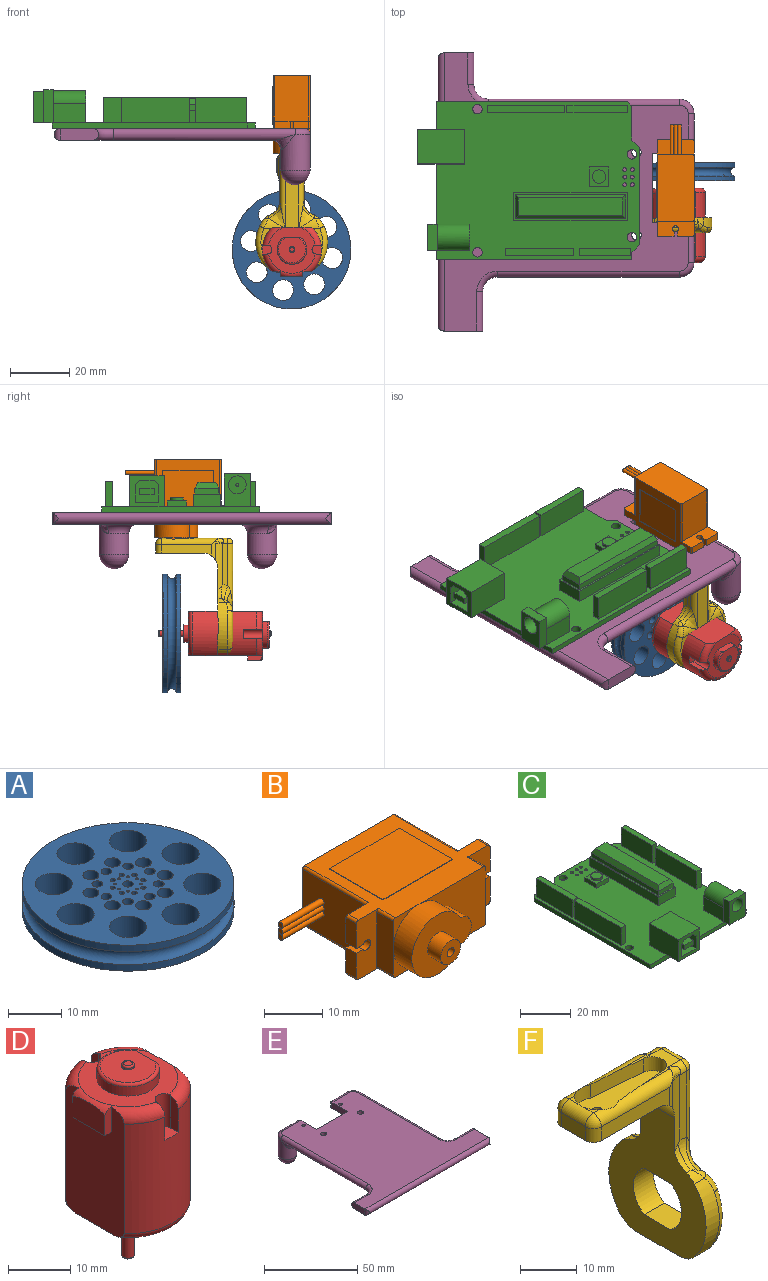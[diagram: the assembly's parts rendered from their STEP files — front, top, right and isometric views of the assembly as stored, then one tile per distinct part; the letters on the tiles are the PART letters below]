
ASSEMBLY  parts=6 mates=5
PART A: 46 faces, bbox 45.6x45.6x6 mm
  f0: cylinder r=20mm len=40mm, axis (0,0,-1), area 188.5mm2, adj f3,f45
  f1: cylinder r=20mm len=40mm, axis (0,0,-1), area 188.5mm2, adj f4,f45
  f2: cylinder r=1mm len=6mm, axis (0,0,-1), area 37.7mm2, adj f3,f4
  f3: plane 40x40mm, normal (0,0,1), area 856.1mm2, adj f0,f2,f5,f6,f7,f8,f9,f10
  f4: plane 40x40mm, normal (0,0,-1), area 856.1mm2, adj f1,f2,f5,f6,f7,f8,f9,f10
  f5: cylinder r=3.5mm len=7mm, axis (0,0,1), area 131.9mm2, adj f3,f4
  f6: cylinder r=3.5mm len=7mm, axis (0,0,1), area 131.9mm2, adj f3,f4
  f7: cylinder r=3.5mm len=7mm, axis (0,0,1), area 131.9mm2, adj f3,f4
  f8: cylinder r=3.5mm len=7mm, axis (0,0,1), area 131.9mm2, adj f3,f4
  f9: cylinder r=3.5mm len=7mm, axis (0,0,1), area 131.9mm2, adj f3,f4
  f10: cylinder r=3.5mm len=7mm, axis (0,0,1), area 131.9mm2, adj f3,f4
  f11: cylinder r=3.5mm len=7mm, axis (0,0,1), area 131.9mm2, adj f3,f4
  f12: cylinder r=3.5mm len=7mm, axis (0,0,1), area 131.9mm2, adj f3,f4
  f13: cylinder r=1.5mm len=6mm, axis (0,0,1), area 56.5mm2, adj f3,f4
  f14: cylinder r=0.5mm len=6mm, axis (0,0,1), area 18.8mm2, adj f3,f4
  f15: cylinder r=0.5mm len=6mm, axis (0,0,1), area 18.8mm2, adj f3,f4
  f16: cylinder r=0.5mm len=6mm, axis (0,0,1), area 18.8mm2, adj f3,f4
  f17: cylinder r=0.5mm len=6mm, axis (0,0,1), area 18.8mm2, adj f3,f4
  f18: cylinder r=0.5mm len=6mm, axis (0,0,1), area 18.8mm2, adj f3,f4
  f19: cylinder r=0.5mm len=6mm, axis (0,0,1), area 18.8mm2, adj f3,f4
  f20: cylinder r=0.5mm len=6mm, axis (0,0,1), area 18.8mm2, adj f3,f4
  f21: cylinder r=0.25mm len=6mm, axis (0,0,1), area 9.4mm2, adj f3,f4
  f22: cylinder r=0.25mm len=6mm, axis (0,0,1), area 9.4mm2, adj f3,f4
  f23: cylinder r=0.25mm len=6mm, axis (0,0,1), area 9.4mm2, adj f3,f4
  f24: cylinder r=0.25mm len=6mm, axis (0,0,1), area 9.4mm2, adj f3,f4
  f25: cylinder r=0.25mm len=6mm, axis (0,0,1), area 9.4mm2, adj f3,f4
  f26: cylinder r=0.25mm len=6mm, axis (0,0,1), area 9.4mm2, adj f3,f4
  f27: cylinder r=0.25mm len=6mm, axis (0,0,1), area 9.4mm2, adj f3,f4
  f28: cylinder r=0.25mm len=6mm, axis (0,0,1), area 9.4mm2, adj f3,f4
  f29: cylinder r=1.5mm len=6mm, axis (0,0,1), area 56.5mm2, adj f3,f4
  f30: cylinder r=1.5mm len=6mm, axis (0,0,1), area 56.5mm2, adj f3,f4
  f31: cylinder r=1.5mm len=6mm, axis (0,0,1), area 56.5mm2, adj f3,f4
  f32: cylinder r=1.5mm len=6mm, axis (0,0,1), area 56.5mm2, adj f3,f4
  f33: cylinder r=1.5mm len=6mm, axis (0,0,1), area 56.5mm2, adj f3,f4
  f34: cylinder r=1.5mm len=6mm, axis (0,0,1), area 56.5mm2, adj f3,f4
  f35: cylinder r=1.5mm len=6mm, axis (0,0,1), area 56.5mm2, adj f3,f4
  f36: cylinder r=1mm len=6mm, axis (0,0,1), area 37.7mm2, adj f3,f4
  f37: cylinder r=0.5mm len=6mm, axis (0,0,1), area 18.8mm2, adj f3,f4
  f38: cylinder r=1mm len=6mm, axis (0,0,1), area 37.7mm2, adj f3,f4
  f39: cylinder r=1mm len=6mm, axis (0,0,1), area 37.7mm2, adj f3,f4
  f40: cylinder r=1mm len=6mm, axis (0,0,1), area 37.7mm2, adj f3,f4
  f41: cylinder r=1mm len=6mm, axis (0,0,1), area 37.7mm2, adj f3,f4
  f42: cylinder r=1mm len=6mm, axis (0,0,1), area 37.7mm2, adj f3,f4
  f43: cylinder r=1mm len=6mm, axis (0,0,1), area 37.7mm2, adj f3,f4
  f44: cylinder r=1mm len=6mm, axis (0,0,1), area 37.7mm2, adj f3,f4
  f45: torus R=20mm, axis (0,0,1), area 563.9mm2, adj f0,f1
PART B: 59 faces, bbox 37.5x29.7x12.7 mm
  f0: plane 31.5x22mm, normal (0,0,-1), area 277mm2, adj f1,f3,f4,f15,f16,f17,f23,f25
  f1: cylinder r=0.5mm len=4mm, axis (0,-1,0), area 3.1mm2, adj f0,f3,f20,f23
  f2: plane 6.25x6.25mm, normal (0,-1,0), area 8.3mm2, adj f5,f7,f18,f47
  f3: plane 16.25x12.5mm, normal (0,-1,0), area 132.6mm2, adj f0,f1,f18,f20,f22,f47,f48
  f4: plane 6.25x6.25mm, normal (0,-1,0), area 8.3mm2, adj f0,f7,f34,f47
  f5: cylinder r=0.5mm len=4mm, axis (0,-1,0), area 3.1mm2, adj f2,f7,f18,f33
  f6: plane 15.5x11.5mm, normal (-1,0,0), area 174.9mm2, adj f8,f12,f13,f14,f15,f16,f17
  f7: plane 11.5x4mm, normal (-1,0,0), area 46mm2, adj f2,f4,f5,f33,f34
  f8: cylinder r=0.6mm len=10mm, axis (-1,0,0), area 37.7mm2, adj f6,f9
  f9: plane 1.2x1.2mm, normal (-1,0,0), area 1.1mm2, adj f8
  f10: plane 1.2x1.2mm, normal (-1,0,0), area 1.1mm2, adj f12
  f11: plane 1.2x1.2mm, normal (-1,0,0), area 1.1mm2, adj f13
  f12: cylinder r=0.6mm len=10mm, axis (-1,0,0), area 37.7mm2, adj f6,f10
  f13: cylinder r=0.6mm len=10mm, axis (-1,0,0), area 37.7mm2, adj f6,f11
  f14: cylinder r=0.5mm len=15.5mm, axis (0,-1,0), area 12.2mm2, adj f6,f15,f17,f18
  f15: plane 22.5x12.5mm, normal (0,1,0), area 281mm2, adj f0,f6,f14,f16,f18,f19,f21,f26
  f16: cylinder r=0.5mm len=15.5mm, axis (0,1,0), area 12.2mm2, adj f0,f6,f15,f17
  f17: plane 12.5x5.5mm, normal (0,1,0), area 57.8mm2, adj f0,f6,f14,f16,f18,f35,f36,f37
  f18: plane 31.5x22mm, normal (0,0,1), area 277mm2, adj f2,f3,f5,f14,f15,f17,f19,f22
  f19: cylinder r=0.5mm len=15.5mm, axis (0,1,0), area 12.2mm2, adj f15,f18,f21,f25
  f20: plane 11.5x4mm, normal (1,0,0), area 46mm2, adj f1,f3,f22,f23
  f21: plane 15.5x11.5mm, normal (1,0,0), area 178.2mm2, adj f15,f19,f25,f26
  f22: cylinder r=0.5mm len=4mm, axis (0,1,0), area 3.1mm2, adj f3,f18,f20,f23
  f23: plane 12.5x5.5mm, normal (0,-1,0), area 57.8mm2, adj f0,f1,f18,f20,f22,f24,f27,f28
  f24: cylinder r=0.5mm len=2.5mm, axis (0,1,0), area 2mm2, adj f18,f23,f25,f28
  f25: plane 12.5x5.5mm, normal (0,1,0), area 57.8mm2, adj f0,f18,f19,f21,f24,f26,f27,f28
  f26: cylinder r=0.5mm len=15.5mm, axis (0,-1,0), area 12.2mm2, adj f0,f15,f21,f25
  f27: cylinder r=0.5mm len=2.5mm, axis (0,-1,0), area 2mm2, adj f0,f23,f25,f29
  f28: plane 5.25x2.5mm, normal (1,0,0), area 13.1mm2, adj f23,f24,f25,f30
  f29: plane 5.25x2.5mm, normal (1,0,0), area 13.1mm2, adj f23,f25,f27,f32
  f30: plane 2.5x1.63mm, normal (0,0,-1), area 4.1mm2, adj f23,f25,f28,f31
  f31: cylinder r=1mm len=2.5mm, axis (0,-1,0), area 13.1mm2, adj f23,f25,f30,f32
  f32: plane 2.5x1.63mm, normal (0,0,1), area 4.1mm2, adj f23,f25,f29,f31
  f33: plane 12.5x5.5mm, normal (0,-1,0), area 57.8mm2, adj f0,f5,f7,f18,f34,f35,f36,f37
  f34: cylinder r=0.5mm len=4mm, axis (0,1,0), area 3.1mm2, adj f0,f4,f7,f33
  f35: cylinder r=0.5mm len=2.5mm, axis (0,1,0), area 2mm2, adj f0,f17,f33,f37
  f36: plane 5.25x2.5mm, normal (-1,0,0), area 13.1mm2, adj f17,f33,f38,f39
  f37: plane 5.25x2.5mm, normal (-1,0,0), area 13.1mm2, adj f17,f33,f35,f41
  f38: cylinder r=0.5mm len=2.5mm, axis (0,-1,0), area 2mm2, adj f17,f18,f33,f36
  f39: plane 2.5x1.63mm, normal (0,0,-1), area 4.1mm2, adj f17,f33,f36,f40
  f40: cylinder r=1mm len=2.5mm, axis (0,-1,0), area 13.1mm2, adj f17,f33,f39,f41
  f41: plane 2.5x1.63mm, normal (0,0,1), area 4.1mm2, adj f17,f33,f37,f40
  f42: plane 13x0.1mm, normal (-1,0,0), area 1.3mm2, adj f18,f43,f45,f46
  f43: plane 17x0.1mm, normal (0,1,0), area 1.7mm2, adj f18,f42,f44,f46
  f44: plane 13x0.1mm, normal (1,0,0), area 1.3mm2, adj f18,f43,f45,f46
  f45: plane 17x0.1mm, normal (0,-1,0), area 1.7mm2, adj f18,f42,f44,f46
  f46: plane 17x13mm, normal (0,0,1), area 221mm2, adj f42,f43,f44,f45
  f47: cylinder r=6.25mm len=12.5mm, axis (0,-1,0), area 150.6mm2, adj f2,f3,f4,f48,f49
  f48: cylinder r=2.8mm len=5.59mm, axis (0,-1,0), area 38.3mm2, adj f3,f47,f49
  f49: plane 14.5x12.5mm, normal (0,-1,0), area 113.7mm2, adj f47,f48,f51
  f50: plane 1.7x1.7mm, normal (0,-1,0), area 2.3mm2, adj f53
  f51: cylinder r=2.4mm len=4.8mm, axis (0,-1,0), area 48.3mm2, adj f49,f52
  f52: plane 4.8x4.8mm, normal (0,-1,0), area 15.8mm2, adj f51,f53
  f53: cylinder r=0.85mm len=3.2mm, axis (0,-1,0), area 17.1mm2, adj f50,f52
  f54: plane 13x0.1mm, normal (-1,0,0), area 1.3mm2, adj f0,f55,f56,f57
  f55: plane 17x0.1mm, normal (0,1,0), area 1.7mm2, adj f0,f54,f56,f58
  f56: plane 17x13mm, normal (0,0,-1), area 221mm2, adj f54,f55,f57,f58
  f57: plane 17x0.1mm, normal (0,-1,0), area 1.7mm2, adj f0,f54,f56,f58
  f58: plane 13x0.1mm, normal (1,0,0), area 1.3mm2, adj f0,f55,f56,f57
PART C: 159 faces, bbox 53.3x75x13 mm
  f0: plane 68.58x53.34mm, normal (0,0,1), area 2744.3mm2, adj f1,f2,f3,f4,f5,f6,f7,f8
  f1: plane 2.54x2.54mm, normal (0.71,0.71,0), area 6.8mm2, adj f0,f2,f51,f52
  f2: plane 32.77x1.9mm, normal (0,1,0), area 62.3mm2, adj f0,f1,f3,f52
  f3: plane 2.54x2.54mm, normal (-0.71,0.71,0), area 6.8mm2, adj f0,f2,f4,f52
  f4: plane 11.43x1.9mm, normal (0,1,0), area 21.7mm2, adj f0,f3,f5,f52
  f5: plane 1.9x1.52mm, normal (-0.71,0.71,0), area 4.1mm2, adj f0,f4,f6,f52
  f6: plane 64.52x1.9mm, normal (-1,0,0), area 122.6mm2, adj f0,f5,f7,f52
  f7: plane 53.34x1.9mm, normal (0,-1,0), area 101.3mm2, adj f0,f6,f8,f52,f81,f99,f107,f108
  f8: plane 66.04x1.9mm, normal (1,0,0), area 125.5mm2, adj f0,f7,f51,f52
  f9: cylinder r=1.59mm len=3.18mm, axis (0,0,-1), area 19mm2, adj f0,f52
  f10: cylinder r=1.59mm len=3.18mm, axis (0,0,-1), area 19mm2, adj f0,f52
  f11: cylinder r=1.59mm len=3.18mm, axis (0,0,-1), area 19mm2, adj f0,f52
  f12: cylinder r=1.59mm len=3.18mm, axis (0,0,-1), area 19mm2, adj f0,f52
  f13: cylinder r=0.64mm len=1.9mm, axis (0,0,-1), area 7.6mm2, adj f52,f80
  f14: cylinder r=0.64mm len=1.9mm, axis (0,0,-1), area 7.6mm2, adj f52,f79
  f15: cylinder r=0.64mm len=1.9mm, axis (0,0,-1), area 7.6mm2, adj f52,f78
  f16: cylinder r=0.64mm len=1.9mm, axis (0,0,-1), area 7.6mm2, adj f52,f77
  f17: cylinder r=0.64mm len=1.9mm, axis (0,0,-1), area 7.6mm2, adj f52,f76
  f18: cylinder r=0.64mm len=1.9mm, axis (0,0,-1), area 7.6mm2, adj f52,f75
  f19: cylinder r=0.64mm len=1.9mm, axis (0,0,-1), area 7.6mm2, adj f52,f74
  f20: cylinder r=0.64mm len=1.9mm, axis (0,0,-1), area 7.6mm2, adj f52,f73
  f21: cylinder r=0.64mm len=1.9mm, axis (0,0,-1), area 7.6mm2, adj f52,f72
  f22: cylinder r=0.64mm len=1.9mm, axis (0,0,-1), area 7.6mm2, adj f52,f71
  f23: cylinder r=0.64mm len=1.9mm, axis (0,0,-1), area 7.6mm2, adj f52,f58
  f24: cylinder r=0.64mm len=1.9mm, axis (0,0,-1), area 7.6mm2, adj f52,f140
  f25: cylinder r=0.64mm len=1.9mm, axis (0,0,-1), area 7.6mm2, adj f52,f151
  f26: cylinder r=0.64mm len=1.9mm, axis (0,0,-1), area 7.6mm2, adj f52,f59
  f27: cylinder r=0.64mm len=1.9mm, axis (0,0,-1), area 7.6mm2, adj f52,f60
  f28: cylinder r=0.64mm len=1.9mm, axis (0,0,-1), area 7.6mm2, adj f52,f61
  f29: cylinder r=0.64mm len=1.9mm, axis (0,0,-1), area 7.6mm2, adj f52,f62
  f30: cylinder r=0.64mm len=1.9mm, axis (0,0,-1), area 7.6mm2, adj f52,f63
  f31: cylinder r=0.64mm len=1.9mm, axis (0,0,-1), area 7.6mm2, adj f52,f64
  f32: cylinder r=0.64mm len=1.9mm, axis (0,0,-1), area 7.6mm2, adj f52,f65
  f33: cylinder r=0.64mm len=1.9mm, axis (0,0,-1), area 7.6mm2, adj f52,f139
  f34: cylinder r=0.64mm len=1.9mm, axis (0,0,-1), area 7.6mm2, adj f52,f138
  f35: cylinder r=0.64mm len=1.9mm, axis (0,0,-1), area 7.6mm2, adj f52,f137
  f36: cylinder r=0.64mm len=1.9mm, axis (0,0,-1), area 7.6mm2, adj f52,f136
  f37: cylinder r=0.64mm len=1.9mm, axis (0,0,-1), area 7.6mm2, adj f52,f135
  f38: cylinder r=0.64mm len=1.9mm, axis (0,0,-1), area 7.6mm2, adj f52,f134
  f39: cylinder r=0.64mm len=1.9mm, axis (0,0,-1), area 7.6mm2, adj f52,f133
  f40: cylinder r=0.64mm len=1.9mm, axis (0,0,-1), area 7.6mm2, adj f52,f150
  f41: cylinder r=0.64mm len=1.9mm, axis (0,0,-1), area 7.6mm2, adj f52,f149
  f42: cylinder r=0.64mm len=1.9mm, axis (0,0,-1), area 7.6mm2, adj f52,f148
  f43: cylinder r=0.64mm len=1.9mm, axis (0,0,-1), area 7.6mm2, adj f52,f147
  f44: cylinder r=0.64mm len=1.9mm, axis (0,0,-1), area 7.6mm2, adj f52,f146
  f45: cylinder r=0.64mm len=1.9mm, axis (0,0,-1), area 7.6mm2, adj f0,f52
  f46: cylinder r=0.64mm len=1.9mm, axis (0,0,-1), area 7.6mm2, adj f0,f52
  f47: cylinder r=0.64mm len=1.9mm, axis (0,0,-1), area 7.6mm2, adj f0,f52
  f48: cylinder r=0.64mm len=1.9mm, axis (0,0,-1), area 7.6mm2, adj f0,f52
  f49: cylinder r=0.64mm len=1.9mm, axis (0,0,-1), area 7.6mm2, adj f0,f52
  f50: cylinder r=0.64mm len=1.9mm, axis (0,0,-1), area 7.6mm2, adj f0,f52
  f51: plane 2.54x1.9mm, normal (0,1,0), area 4.8mm2, adj f0,f1,f8,f52
  f52: plane 68.58x53.34mm, normal (0,0,-1), area 3531.3mm2, adj f1,f2,f3,f4,f5,f6,f7,f8
  f53: plane 20.48x2.5mm, normal (0,0,1), area 51.2mm2, adj f54,f55,f56,f57
  f54: plane 8.6x2.5mm, normal (0,1,0), area 21.5mm2, adj f0,f53,f55,f57
  f55: plane 20.48x8.6mm, normal (1,0,0), area 176.1mm2, adj f0,f53,f54,f56
  f56: plane 8.6x2.5mm, normal (0,-1,0), area 21.5mm2, adj f0,f53,f55,f57
  f57: plane 20.48x8.6mm, normal (-1,0,0), area 176.1mm2, adj f0,f53,f54,f56
  f58: plane 1.27x1.27mm, normal (0,0,-1), area 1.3mm2, adj f23
  f59: plane 1.27x1.27mm, normal (0,0,-1), area 1.3mm2, adj f26
  f60: plane 1.27x1.27mm, normal (0,0,-1), area 1.3mm2, adj f27
  f61: plane 1.27x1.27mm, normal (0,0,-1), area 1.3mm2, adj f28
  f62: plane 1.27x1.27mm, normal (0,0,-1), area 1.3mm2, adj f29
  f63: plane 1.27x1.27mm, normal (0,0,-1), area 1.3mm2, adj f30
  f64: plane 1.27x1.27mm, normal (0,0,-1), area 1.3mm2, adj f31
  f65: plane 1.27x1.27mm, normal (0,0,-1), area 1.3mm2, adj f32
  f66: plane 26x2.5mm, normal (0,0,1), area 65mm2, adj f67,f68,f69,f70
  f67: plane 26x8.6mm, normal (1,0,0), area 223.6mm2, adj f0,f66,f68,f70
  f68: plane 8.6x2.5mm, normal (0,-1,0), area 21.5mm2, adj f0,f66,f67,f69
  f69: plane 26x8.6mm, normal (-1,0,0), area 223.6mm2, adj f0,f66,f68,f70
  f70: plane 8.6x2.5mm, normal (0,1,0), area 21.5mm2, adj f0,f66,f67,f69
  f71: plane 1.27x1.27mm, normal (0,0,-1), area 1.3mm2, adj f22
  f72: plane 1.27x1.27mm, normal (0,0,-1), area 1.3mm2, adj f21
  f73: plane 1.27x1.27mm, normal (0,0,-1), area 1.3mm2, adj f20
  f74: plane 1.27x1.27mm, normal (0,0,-1), area 1.3mm2, adj f19
  f75: plane 1.27x1.27mm, normal (0,0,-1), area 1.3mm2, adj f18
  f76: plane 1.27x1.27mm, normal (0,0,-1), area 1.3mm2, adj f17
  f77: plane 1.27x1.27mm, normal (0,0,-1), area 1.3mm2, adj f16
  f78: plane 1.27x1.27mm, normal (0,0,-1), area 1.3mm2, adj f15
  f79: plane 1.27x1.27mm, normal (0,0,-1), area 1.3mm2, adj f14
  f80: plane 1.27x1.27mm, normal (0,0,-1), area 1.3mm2, adj f13
  f81: plane 11.6x6.38mm, normal (0,0,-1), area 73.9mm2, adj f7,f82,f83,f85
  f82: plane 11.6x10.5mm, normal (0,-1,0), area 64.6mm2, adj f81,f83,f85,f86,f87,f88,f89,f90
  f83: plane 16x10.5mm, normal (1,0,0), area 168mm2, adj f0,f81,f82,f84,f86
  f84: plane 11.6x10.5mm, normal (0,1,0), area 121.8mm2, adj f0,f83,f85,f86
  f85: plane 16x10.5mm, normal (-1,0,0), area 168mm2, adj f0,f81,f82,f84,f86
  f86: plane 16x11.6mm, normal (0,0,1), area 185.6mm2, adj f82,f83,f84,f85
  f87: plane 14.14x5.02mm, normal (0,0,-1), area 71mm2, adj f82,f88,f92,f93
  f88: plane 14.14x1.44mm, normal (0.71,0,-0.71), area 28.8mm2, adj f82,f87,f89,f93
  f89: plane 14.14x6.06mm, normal (1,0,0), area 85.7mm2, adj f82,f88,f90,f93
  f90: plane 14.14x7.9mm, normal (0,0,1), area 111.7mm2, adj f82,f89,f91,f93
  f91: plane 14.14x6.06mm, normal (-1,0,0), area 85.7mm2, adj f82,f90,f92,f93
  f92: plane 14.14x1.44mm, normal (-0.71,0,-0.71), area 28.8mm2, adj f82,f87,f91,f93
  f93: plane 7.9x7.5mm, normal (0,-1,0), area 47mm2, adj f87,f88,f89,f90,f91,f92,f95,f96
  f94: plane 4.88x2.08mm, normal (0,-1,0), area 10.2mm2, adj f95,f96,f97,f98
  f95: plane 14.14x4.88mm, normal (0,0,1), area 69mm2, adj f93,f94,f96,f98
  f96: plane 14.14x2.08mm, normal (-1,0,0), area 29.4mm2, adj f93,f94,f95,f97
  f97: plane 14.14x4.88mm, normal (0,0,-1), area 69mm2, adj f93,f94,f96,f98
  f98: plane 14.14x2.08mm, normal (1,0,0), area 29.4mm2, adj f93,f94,f95,f97
  f99: plane 8.88x2.88mm, normal (0,0,-1), area 25.5mm2, adj f7,f107,f108,f109
  f100: plane 11x6.49mm, normal (1,0,0), area 71.4mm2, adj f0,f101,f103,f104
  f101: cylinder r=4.44mm len=11mm, axis (0,-1,0), area 153.4mm2, adj f100,f102,f103,f104,f105
  f102: plane 11x6.49mm, normal (-1,0,0), area 71.4mm2, adj f0,f101,f103,f105
  f103: plane 10.93x8.88mm, normal (0,1,0), area 88.6mm2, adj f0,f100,f101,f102
  f104: plane 6.63x0mm, normal (0,-1,0), area 0mm2, adj f0,f100,f101,f108
  f105: plane 11.12x8.88mm, normal (0,1,0), area 10.1mm2, adj f0,f101,f102,f106,f107,f108
  f106: plane 8.88x3.3mm, normal (0,0,1), area 29.3mm2, adj f105,f107,f108,f109
  f107: plane 11.13x3.3mm, normal (-1,0,0), area 36.7mm2, adj f0,f7,f99,f105,f106,f109
  f108: plane 11.13x3.3mm, normal (1,0,0), area 36.7mm2, adj f0,f7,f99,f104,f105,f106,f109
  f109: plane 11.13x8.88mm, normal (0,-1,0), area 70.5mm2, adj f99,f106,f107,f108,f110
  f110: cylinder r=3mm len=12.8mm, axis (0,-1,0), area 241.3mm2, adj f109,f111
  f111: plane 6x6mm, normal (0,-1,0), area 27.5mm2, adj f110,f112
  f112: cylinder r=0.5mm len=10mm, axis (0,1,0), area 31.4mm2, adj f111,f113
  f113: sphere r=0.5mm, area 1.6mm2, adj f112
  f114: plane 9.33x4.3mm, normal (0,-1,0), area 40.1mm2, adj f0,f115,f117,f118
  f115: plane 38.37x4.3mm, normal (1,0,0), area 164.8mm2, adj f0,f114,f116,f118
  f116: plane 9.33x4.3mm, normal (0,1,0), area 40.1mm2, adj f0,f115,f117,f118
  f117: plane 38.37x4.3mm, normal (-1,0,0), area 164.8mm2, adj f0,f114,f116,f118
  f118: plane 38.37x9.33mm, normal (0,0,1), area 57.4mm2, adj f114,f115,f116,f117,f119,f120,f121,f122
  f119: plane 37.19x2mm, normal (-1,0,0), area 74.4mm2, adj f118,f120,f122,f127
  f120: plane 8.08x2mm, normal (0,-1,0), area 16.2mm2, adj f118,f119,f121,f126
  f121: plane 37.19x2mm, normal (1,0,0), area 74.4mm2, adj f118,f120,f122,f125
  f122: plane 8.08x2mm, normal (0,1,0), area 16.2mm2, adj f118,f119,f121,f124
  f123: plane 35.16x6.05mm, normal (0,0,1), area 212.7mm2, adj f124,f125,f126,f127
  f124: plane 8.08x2mm, normal (0,0.9,0.44), area 15.7mm2, adj f122,f123,f125,f127
  f125: plane 37.19x2mm, normal (0.89,0,0.45), area 81.1mm2, adj f121,f123,f124,f126
  f126: plane 8.08x2mm, normal (0,-0.88,0.47), area 16mm2, adj f120,f123,f125,f127
  f127: plane 37.19x2mm, normal (-0.89,0,0.45), area 81.2mm2, adj f119,f123,f124,f126
  f128: plane 23x2.44mm, normal (0,0,1), area 56mm2, adj f129,f130,f131,f132
  f129: plane 23x8.6mm, normal (1,0,0), area 197.8mm2, adj f0,f128,f130,f132
  f130: plane 8.6x2.44mm, normal (0,-1,0), area 20.9mm2, adj f0,f128,f129,f131
  f131: plane 23x8.6mm, normal (-1,0,0), area 197.8mm2, adj f0,f128,f130,f132
  f132: plane 8.6x2.44mm, normal (0,1,0), area 20.9mm2, adj f0,f128,f129,f131
  f133: plane 1.27x1.27mm, normal (0,0,-1), area 1.3mm2, adj f39
  f134: plane 1.27x1.27mm, normal (0,0,-1), area 1.3mm2, adj f38
  f135: plane 1.27x1.27mm, normal (0,0,-1), area 1.3mm2, adj f37
  f136: plane 1.27x1.27mm, normal (0,0,-1), area 1.3mm2, adj f36
  f137: plane 1.27x1.27mm, normal (0,0,-1), area 1.3mm2, adj f35
  f138: plane 1.27x1.27mm, normal (0,0,-1), area 1.3mm2, adj f34
  f139: plane 1.27x1.27mm, normal (0,0,-1), area 1.3mm2, adj f33
  f140: plane 1.27x1.27mm, normal (0,0,-1), area 1.3mm2, adj f24
  f141: plane 17.27x2.44mm, normal (0,0,1), area 42.1mm2, adj f142,f143,f144,f145
  f142: plane 8.6x2.44mm, normal (0,-1,0), area 20.9mm2, adj f0,f141,f143,f145
  f143: plane 17.27x8.6mm, normal (-1,0,0), area 148.6mm2, adj f0,f141,f142,f144
  f144: plane 8.6x2.44mm, normal (0,1,0), area 20.9mm2, adj f0,f141,f143,f145
  f145: plane 17.27x8.6mm, normal (1,0,0), area 148.6mm2, adj f0,f141,f142,f144
  f146: plane 1.27x1.27mm, normal (0,0,-1), area 1.3mm2, adj f44
  f147: plane 1.27x1.27mm, normal (0,0,-1), area 1.3mm2, adj f43
  f148: plane 1.27x1.27mm, normal (0,0,-1), area 1.3mm2, adj f42
  f149: plane 1.27x1.27mm, normal (0,0,-1), area 1.3mm2, adj f41
  f150: plane 1.27x1.27mm, normal (0,0,-1), area 1.3mm2, adj f40
  f151: plane 1.27x1.27mm, normal (0,0,-1), area 1.3mm2, adj f25
  f152: plane 6.5x2mm, normal (-1,0,0), area 13mm2, adj f0,f153,f155,f156
  f153: plane 6.5x2mm, normal (0,-1,0), area 13mm2, adj f0,f152,f154,f156
  f154: plane 6.5x2mm, normal (1,0,0), area 13mm2, adj f0,f153,f155,f156
  f155: plane 6.5x2mm, normal (0,1,0), area 13mm2, adj f0,f152,f154,f156
  f156: plane 6.5x6.5mm, normal (0,0,1), area 26.4mm2, adj f152,f153,f154,f155,f157
  f157: cylinder r=2.24mm len=4.49mm, axis (0,0,-1), area 14.1mm2, adj f156,f158
  f158: plane 4.49x4.49mm, normal (0,0,1), area 15.8mm2, adj f157
PART D: 35 faces, bbox 21.1x21.8x38 mm
  f0: plane 15.74x15.5mm, normal (0,0,1), area 119.4mm2, adj f4,f10,f11,f22,f26,f29,f30,f31
  f1: cylinder r=10mm len=21.5mm, axis (0,0,-1), area 351.1mm2, adj f4,f5,f23,f24,f25,f27,f29,f30
  f2: plane 17x15mm, normal (0,0,-1), area 187.9mm2, adj f4,f5,f6,f27,f28
  f3: cylinder r=10mm len=21.5mm, axis (0,0,-1), area 351.1mm2, adj f4,f5,f19,f20,f21,f28,f30,f31
  f4: plane 25x13.23mm, normal (1,0,0), area 326.4mm2, adj f0,f1,f2,f3,f27,f28,f29,f31
  f5: plane 24.97x13.23mm, normal (-1,0,0), area 289.4mm2, adj f1,f2,f3,f15,f17,f18,f27,f28
  f6: cylinder r=3mm len=6mm, axis (0,0,1), area 28.3mm2, adj f2,f7
  f7: plane 6x6mm, normal (0,0,-1), area 25.1mm2, adj f6,f8
  f8: cylinder r=1mm len=8.2mm, axis (0,0,1), area 51.5mm2, adj f7,f33
  f9: plane 1.4x1.4mm, normal (0,0,-1), area 1.5mm2, adj f33
  f10: plane 6x2.3mm, normal (1,0,0), area 13.6mm2, adj f0,f11,f12,f34
  f11: cylinder r=5mm len=10mm, axis (0,0,-1), area 45mm2, adj f0,f10,f34
  f12: plane 9x8.5mm, normal (0,0,1), area 59.1mm2, adj f10,f13,f34
  f13: cylinder r=1mm len=2mm, axis (0,0,-1), area 1.9mm2, adj f12,f32
  f14: plane 1.4x1.4mm, normal (0,0,1), area 1.5mm2, adj f32
  f15: plane 5.11x1.64mm, normal (0,1,0), area 7mm2, adj f5,f16,f18,f30
  f16: plane 7.4x4.73mm, normal (-1,0,0), area 33.6mm2, adj f15,f17,f18,f30
  f17: plane 5.11x1.64mm, normal (0,-1,0), area 7mm2, adj f5,f16,f18,f30
  f18: plane 7.4x1.5mm, normal (0,0,-1), area 11.1mm2, adj f5,f15,f16,f17
  f19: plane 6.6x1.78mm, normal (-1,0,0), area 9.8mm2, adj f3,f21,f22,f31
  f20: plane 6.6x1.78mm, normal (1,0,0), area 9.8mm2, adj f3,f21,f22,f30
  f21: plane 3.25x3mm, normal (0,0,1), area 8.7mm2, adj f3,f19,f20,f22
  f22: cylinder r=1.5mm len=6.5mm, axis (0,0,1), area 30.6mm2, adj f0,f19,f20,f21,f30,f31
  f23: plane 6.6x1.78mm, normal (1,0,0), area 9.8mm2, adj f1,f25,f26,f30
  f24: plane 6.6x1.78mm, normal (-1,0,0), area 9.8mm2, adj f1,f25,f26,f29
  f25: plane 3.25x3mm, normal (0,0,1), area 8.7mm2, adj f1,f23,f24,f26
  f26: cylinder r=1.5mm len=6.5mm, axis (0,0,1), area 30.6mm2, adj f0,f23,f24,f25,f29,f30
  f27: torus R=8.5mm, axis (0,0,1), area 41mm2, adj f1,f2,f4,f5
  f28: torus R=8.5mm, axis (0,0,1), area 41mm2, adj f2,f3,f4,f5
  f29: torus R=8mm, axis (0,0,1), area 22.8mm2, adj f0,f1,f4,f24,f26
  f30: torus R=8mm, axis (0,0,1), area 55.9mm2, adj f0,f1,f3,f5,f15,f16,f17,f20
  f31: torus R=8mm, axis (0,0,1), area 22.8mm2, adj f0,f3,f4,f19,f22
  f32: torus R=0.7mm, axis (0,0,1), area 2.6mm2, adj f13,f14
  f33: torus R=0.7mm, axis (0,0,-1), area 2.6mm2, adj f8,f9
  f34: torus R=4.5mm, axis (0,0,1), area 19.3mm2, adj f10,f11,f12
PART E: 36 faces, bbox 93.8x86.7x19 mm
  f0: plane 93.76x82.29mm, normal (0,0,-1), area 4476.7mm2, adj f1,f2,f3,f4,f5,f6,f7,f11
  f1: plane 13x4mm, normal (1,0,0), area 50.3mm2, adj f0,f8,f20,f27
  f2: plane 12x4mm, normal (-1,0,0), area 48mm2, adj f0,f3,f8,f15
  f3: plane 23.5x4mm, normal (0,1,0), area 94mm2, adj f0,f2,f4,f8
  f4: plane 12x4mm, normal (1,0,0), area 48mm2, adj f0,f3,f8,f22
  f5: cylinder r=1mm len=4mm, axis (0,0,-1), area 25.1mm2, adj f0,f8
  f6: plane 10.06x4mm, normal (-1,0,0), area 38.5mm2, adj f0,f8,f26,f29
  f7: cylinder r=1mm len=4mm, axis (0,0,-1), area 25.1mm2, adj f0,f8
  f8: plane 93.76x82.29mm, normal (0,0,1), area 4685.1mm2, adj f1,f2,f3,f4,f5,f6,f7,f11
  f9: cylinder r=5mm len=12mm, axis (0,0,-1), area 281.4mm2, adj f14,f17,f30,f31,f32
  f10: cylinder r=5mm len=12mm, axis (0,0,1), area 281.4mm2, adj f13,f24,f33,f34,f35
  f11: cylinder r=1.59mm len=4mm, axis (0,0,1), area 39.9mm2, adj f0,f8
  f12: cylinder r=1.59mm len=4mm, axis (0,0,1), area 39.9mm2, adj f0,f8
  f13: sphere r=5mm, area 157.1mm2, adj f10
  f14: sphere r=5mm, area 157.1mm2, adj f9
  f15: cylinder r=2mm len=4mm, axis (0,0,1), area 8mm2, adj f2,f16
  f16: cylinder r=2mm len=13.25mm, axis (-1,0,0), area 65.2mm2, adj f0,f8,f15,f17,f30
  f17: torus R=3mm, axis (0,0,1), area 21.1mm2, adj f8,f9,f16,f18
  f18: cylinder r=2mm len=61.29mm, axis (0,1,0), area 371.6mm2, adj f0,f8,f17,f19,f32
  f19: torus R=7mm, axis (0,0,1), area 56.5mm2, adj f0,f8,f18,f20
  f20: cylinder r=2mm len=13.21mm, axis (-1,0,0), area 83mm2, adj f0,f1,f8,f19
  f21: cylinder r=2mm len=13.25mm, axis (-1,0,0), area 65.2mm2, adj f0,f8,f22,f24,f33
  f22: cylinder r=2mm len=4mm, axis (0,0,-1), area 8mm2, adj f4,f21
  f23: cylinder r=2mm len=64.24mm, axis (0,-1,0), area 390.1mm2, adj f0,f8,f24,f25,f35
  f24: torus R=3mm, axis (0,0,1), area 21.1mm2, adj f8,f10,f21,f23
  f25: torus R=7mm, axis (0,0,1), area 56.5mm2, adj f0,f8,f23,f26
  f26: cylinder r=2mm len=10.56mm, axis (-1,0,0), area 66.3mm2, adj f0,f6,f8,f25
  f27: cylinder r=2mm len=4mm, axis (0,0,-1), area 8mm2, adj f1,f28
  f28: cylinder r=2mm len=93.76mm, axis (-1,0,0), area 580mm2, adj f0,f8,f27,f29
  f29: cylinder r=2mm len=4mm, axis (0,0,1), area 8mm2, adj f6,f28
  f30: bspline ~7.73x5mm, area 16.9mm2, adj f9,f16,f31
  f31: torus R=8mm, axis (0,0,1), area 67.1mm2, adj f0,f9,f30,f32
  f32: bspline ~7.73x5mm, area 16.9mm2, adj f9,f18,f31
  f33: bspline ~7.73x5mm, area 16.9mm2, adj f10,f21,f34
  f34: torus R=8mm, axis (0,0,1), area 67.1mm2, adj f0,f10,f33,f35
  f35: bspline ~7.73x5mm, area 16.9mm2, adj f10,f23,f34
PART F: 73 faces, bbox 26.4x26.6x40.1 mm
  f0: plane 22.93x4.6mm, normal (1,0,0), area 105.5mm2, adj f11,f32,f33,f34
  f1: plane 10.74x6.35mm, normal (0,0,1), area 16.6mm2, adj f19,f21,f22,f34,f36,f38,f41,f47
  f2: plane 2.47x1.32mm, normal (0,0,1), area 1.2mm2, adj f20,f41,f44
  f3: cylinder r=12.12mm len=15.74mm, axis (-1,0,0), area 55.4mm2, adj f14,f25,f29,f48,f49
  f4: plane 10.84x3.3mm, normal (0,0,-1), area 35.8mm2, adj f14,f25,f26,f30
  f5: cylinder r=12.12mm len=15.74mm, axis (-1,0,0), area 55.4mm2, adj f14,f26,f27,f52,f54
  f6: plane 14.35x1.7mm, normal (0,1,0), area 24mm2, adj f33,f38,f56,f69
  f7: plane 2.47x1.32mm, normal (0,0,1), area 1.2mm2, adj f20,f44,f47
  f8: cylinder r=6mm len=10mm, axis (-1,0,0), area 59.1mm2, adj f9,f11,f13,f14,f55
  f9: plane 6.63x5mm, normal (0,0,1), area 33.2mm2, adj f8,f10,f13,f14
  f10: cylinder r=6mm len=10mm, axis (-1,0,0), area 59.1mm2, adj f9,f11,f13,f14,f51
  f11: plane 6.78x5.15mm, normal (0,0,-1), area 33.1mm2, adj f0,f8,f10,f14,f32,f33,f51,f55
  f12: plane 14.35x1.7mm, normal (0,-1,0), area 24mm2, adj f32,f36,f60,f66
  f13: plane 20.85x12.55mm, normal (1,0,0), area 138.8mm2, adj f8,f9,f10,f27,f28,f29,f30,f31
  f14: plane 29.45x24.45mm, normal (-1,0,0), area 395.3mm2, adj f3,f4,f5,f8,f9,f10,f11,f25
  f15: plane 17x4mm, normal (0,-1,0), area 52mm2, adj f17,f43,f46,f47,f72
  f16: plane 17x4mm, normal (0,1,0), area 52mm2, adj f17,f39,f40,f41,f72
  f17: plane 16x10mm, normal (0,0,-1), area 155.1mm2, adj f15,f16,f18,f24,f40,f43,f72
  f18: plane 6x3mm, normal (-1,0,0), area 18mm2, adj f17,f40,f43,f44
  f19: plane 12.06x3.05mm, normal (-0.08,-1,0), area 36mm2, adj f1,f20,f22,f23,f41
  f20: cylinder r=4mm len=8mm, axis (0,0,1), area 49.5mm2, adj f2,f7,f19,f21,f23,f41,f44,f47
  f21: plane 12.06x3.05mm, normal (-0.08,1,0), area 36mm2, adj f1,f20,f22,f23,f47
  f22: cylinder r=2.51mm len=5mm, axis (0,0,1), area 22.4mm2, adj f1,f19,f21,f23
  f23: plane 20.24x8mm, normal (0,0,1), area 117.7mm2, adj f19,f20,f21,f22,f24
  f24: cylinder r=1mm len=2mm, axis (0,0,1), area 12.6mm2, adj f17,f23
  f25: cylinder r=5mm len=3.8mm, axis (-1,0,0), area 14.3mm2, adj f3,f4,f14,f31
  f26: cylinder r=5mm len=3.8mm, axis (-1,0,0), area 14.3mm2, adj f4,f5,f14,f28
  f27: torus R=10.43mm, axis (1,0,0), area 35.8mm2, adj f5,f13,f28,f54
  f28: torus R=3.3mm, axis (1,0,0), area 10.1mm2, adj f13,f26,f27,f30
  f29: torus R=10.43mm, axis (1,0,0), area 35.8mm2, adj f3,f13,f31,f49
  f30: cylinder r=1.7mm len=10.84mm, axis (0,-1,0), area 28.9mm2, adj f4,f13,f28,f31
  f31: torus R=3.3mm, axis (1,0,0), area 10.1mm2, adj f13,f25,f29,f30
  f32: cylinder r=1.7mm len=23.03mm, axis (0,0,1), area 47.8mm2, adj f0,f11,f12,f35,f64,f65
  f33: cylinder r=1.7mm len=23.03mm, axis (0,0,-1), area 47.8mm2, adj f0,f6,f11,f37,f67,f68
  f34: cylinder r=1.7mm len=4.8mm, axis (0,1,0), area 12.6mm2, adj f0,f1,f35,f37
  f35: bspline ~2.13x1.7mm, area 3mm2, adj f32,f34,f36
  f36: cylinder r=1.6mm len=3.3mm, axis (-1,0,0), area 4.4mm2, adj f1,f12,f35,f61,f62,f63
  f37: bspline ~1.81x1.7mm, area 3mm2, adj f33,f34,f38
  f38: cylinder r=1.6mm len=3.3mm, axis (1,0,0), area 4.4mm2, adj f1,f6,f37,f57,f58,f59
  f39: cylinder r=2mm len=6.09mm, axis (0,0,-1), area 5.5mm2, adj f16,f41,f56,f57,f72
  f40: cylinder r=2mm len=3mm, axis (0,0,1), area 9.4mm2, adj f16,f17,f18,f42
  f41: cylinder r=2mm len=19mm, axis (-1,0,0), area 52mm2, adj f1,f2,f16,f19,f20,f39,f42,f58
  f42: sphere r=2mm, area 8.6mm2, adj f40,f41,f44
  f43: cylinder r=2mm len=3mm, axis (0,0,-1), area 9.4mm2, adj f15,f17,f18,f45
  f44: cylinder r=2mm len=6mm, axis (0,1,0), area 18.8mm2, adj f2,f7,f18,f20,f42,f45
  f45: sphere r=2mm, area 6.3mm2, adj f43,f44,f47
  f46: cylinder r=2mm len=6.09mm, axis (0,0,1), area 5.5mm2, adj f15,f47,f60,f61,f72
  f47: cylinder r=2mm len=19mm, axis (1,0,0), area 52mm2, adj f1,f7,f15,f20,f21,f45,f46,f62
  f48: cylinder r=5mm len=2.51mm, axis (-1,0,0), area 4.6mm2, adj f3,f14,f50,f71
  f49: bspline ~4.95x3.57mm, area 8.3mm2, adj f3,f29,f50,f51
  f50: bspline ~3.11x3.11mm, area 2.7mm2, adj f48,f49,f51,f65,f66
  f51: cylinder r=5mm len=6.43mm, axis (0,1,0), area 12.5mm2, adj f10,f11,f13,f49,f50,f64
  f52: cylinder r=5mm len=2.51mm, axis (-1,0,0), area 4.6mm2, adj f5,f14,f53,f70
  f53: bspline ~3.11x3.11mm, area 2.7mm2, adj f52,f54,f55,f68,f69
  f54: bspline ~4.95x3.57mm, area 8.3mm2, adj f5,f27,f53,f55
  f55: cylinder r=5mm len=6.43mm, axis (0,1,0), area 12.5mm2, adj f8,f11,f13,f53,f54,f67
  f56: cylinder r=5mm len=15.78mm, axis (0,0,-1), area 31.8mm2, adj f6,f14,f39,f57,f69,f70,f72
  f57: bspline ~2.93x2.67mm, area 1.1mm2, adj f38,f39,f56,f58
  f58: bspline ~3x2.31mm, area 4.4mm2, adj f38,f41,f57,f59
  f59: bspline ~1.13x0.98mm, area 0.1mm2, adj f1,f38,f58
  f60: cylinder r=5mm len=15.78mm, axis (0,0,1), area 31.8mm2, adj f12,f14,f46,f61,f66,f71,f72
  f61: bspline ~2.93x2.67mm, area 1.1mm2, adj f36,f46,f60,f62
  f62: bspline ~3.03x2.33mm, area 4.4mm2, adj f36,f47,f61,f63
  f63: bspline ~1.13x0.98mm, area 0.1mm2, adj f1,f36,f62
  f64: bspline ~7.88x6.07mm, area 16.9mm2, adj f11,f32,f51,f65
  f65: bspline ~6.37x4.31mm, area 8.4mm2, adj f32,f50,f64,f66
  f66: bspline ~5.12x3.75mm, area 8.8mm2, adj f12,f50,f60,f65,f71
  f67: bspline ~7.88x6.07mm, area 16.9mm2, adj f11,f33,f55,f68
  f68: bspline ~6.34x4.31mm, area 8.4mm2, adj f33,f53,f67,f69
  f69: bspline ~5.12x3.75mm, area 8.8mm2, adj f6,f53,f56,f68,f70
  f70: bspline ~4.39x3.2mm, area 6mm2, adj f14,f52,f56,f69
  f71: bspline ~4.41x3.2mm, area 6mm2, adj f14,f48,f60,f66
  f72: cylinder r=5mm len=10mm, axis (0,1,0), area 74.9mm2, adj f14,f15,f16,f17,f39,f46,f56,f60
PLACE A rot(axis=(0.36,-0.66,0.66),140.9deg) t=(-2.55,18.29,-9.57)mm
PLACE B rot(axis=(0.58,-0.58,-0.58),120deg) t=(3.71,9.77,31.26)mm
PLACE C rot(axis=(0,0,-1),90deg) t=(-50.27,12.24,31.26)mm
PLACE D rot(axis=(0.58,-0.58,0.58),120.2deg) t=(-2.51,9.69,-9.57)mm
PLACE E rot(axis=(0,0,-1),90deg) t=(-39.43,9.77,27.26)mm fixed
PLACE F rot(axis=(0,0,-1),89.7deg) t=(-2.47,-0.26,-7.07)mm
MATE revolute B.f47 <-> F.f20  axis (0,0,-1) through (-2.54,14.77,19.56)mm
MATE fastened E.f7 <-> B.f31  axis (0,0,1) through (-2.54,-3.98,31.26)mm
MATE fastened F.f11 <-> D.f4  axis (0,0,-1) through (-2.45,-2.76,-2.07)mm
MATE fastened C.f52 <-> E.f8  axis (0,0,-1) through (-49.66,12.08,31.26)mm
MATE revolute A.f2 <-> D.f8  axis (0,1,0) through (-2.54,15.29,-9.57)mm
